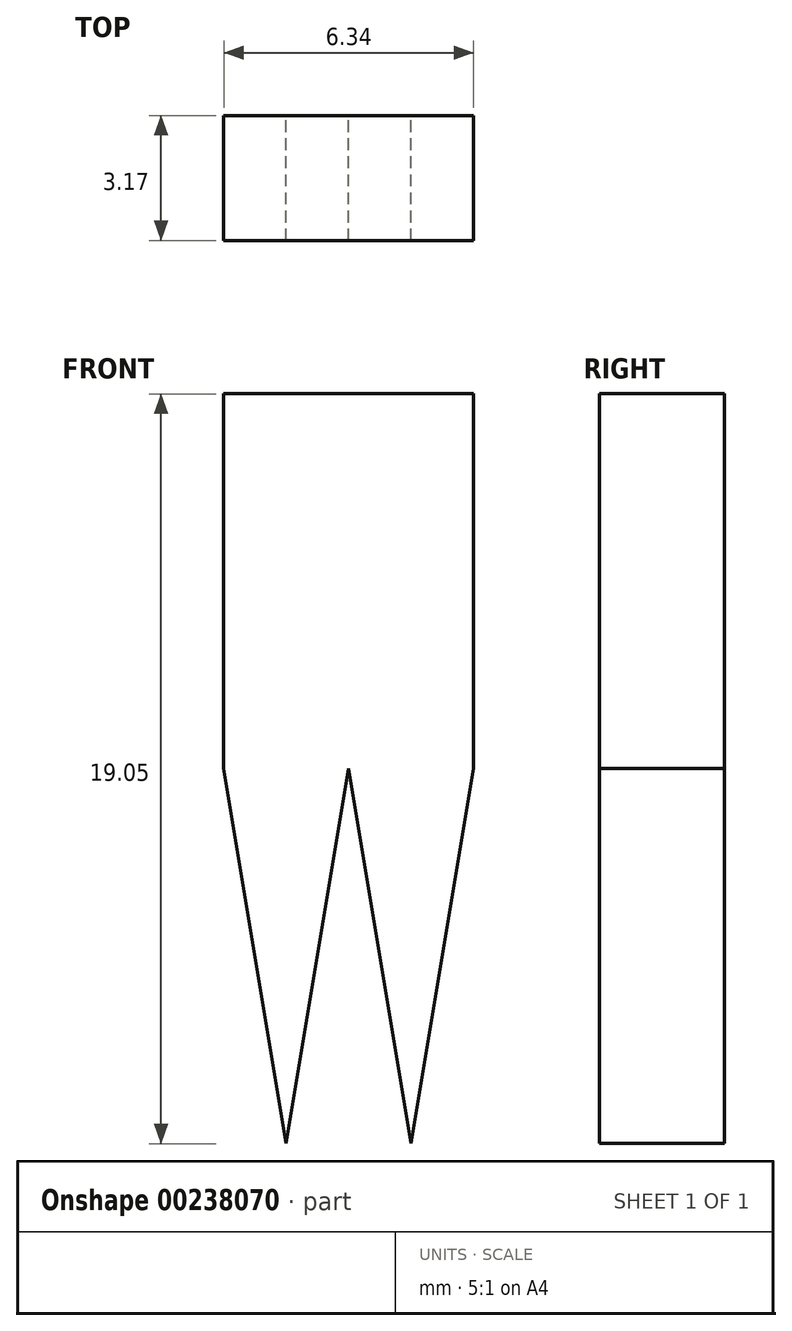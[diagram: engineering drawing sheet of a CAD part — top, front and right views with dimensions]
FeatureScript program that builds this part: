
annotation { "Feature Type Name" : "Feature", "Feature Type Description" : "" }
export const myFeature = defineFeature(function(context is Context, id is Id, definition is map)
    precondition{}
    {
        {
            var Q0;
            Q0=qCreatedBy(makeId("Front.planeOp"),FACE);
            var sketch = newSketch(context, id + "F0", { "sketchPlane" : qUnion([Q0])});
            skLineSegment(sketch, "E0.bottom", {"start": v(3.17, -4.76) * mm, "end": v(-3.18, -4.76) * mm});
            skLineSegment(sketch, "E0.top", {"start": v(3.18, 4.76) * mm, "end": v(-3.17, 4.76) * mm});
            skLineSegment(sketch, "E0.left", {"start": v(3.17, -4.76) * mm, "end": v(3.18, 4.76) * mm});
            skLineSegment(sketch, "E0.right", {"start": v(-3.18, -4.76) * mm, "end": v(-3.17, 4.76) * mm});
            skPoint(sketch, "E0.middle", {"position": v(0, 0) * mm});
            skLineSegment(sketch, "E1.0", {"start": v(-3.18, -4.76) * mm, "end": v(0, -4.76) * mm});
            skLineSegment(sketch, "E1.1", {"start": v(0, -4.76) * mm, "end": v(-1.59, -14.29) * mm});
            skLineSegment(sketch, "E1.2", {"start": v(-1.59, -14.29) * mm, "end": v(-3.18, -4.76) * mm});
            skLineSegment(sketch, "E2.0", {"start": v(0, -4.76) * mm, "end": v(1.59, -14.29) * mm});
            skLineSegment(sketch, "E2.1", {"start": v(1.59, -14.29) * mm, "end": v(3.18, -4.76) * mm});
            skLineSegment(sketch, "E2.2", {"start": v(3.17, -4.76) * mm, "end": v(0, -4.76) * mm});
            skSolve(sketch);
        }
        {
            var Q0;
            Q0 = qSketchRegion(id + "F0", true);
            extrude(context, id + "F1", {"entities" : qUnion([Q0]), "depth" : 3.17 * mm});
        }
    });
